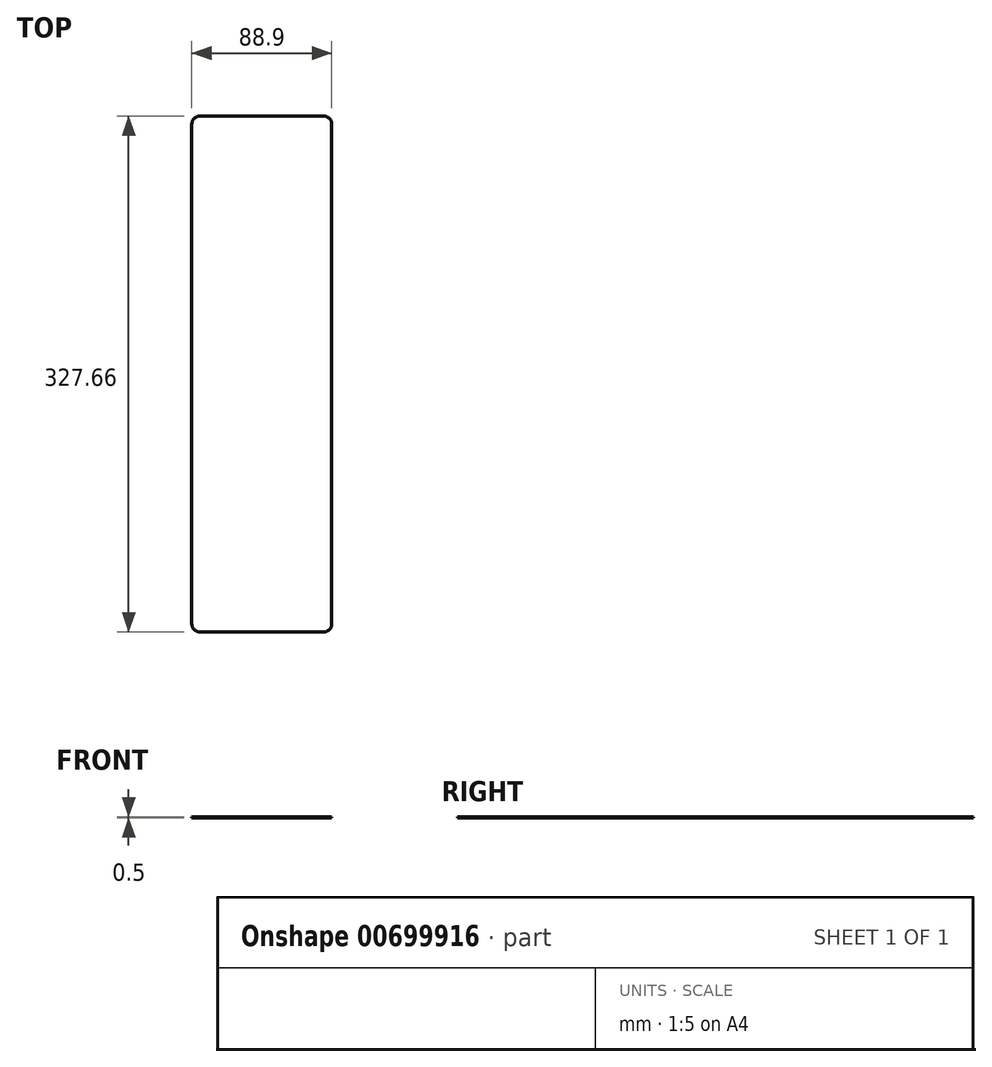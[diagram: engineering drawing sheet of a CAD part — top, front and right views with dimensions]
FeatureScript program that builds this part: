
annotation { "Feature Type Name" : "Feature", "Feature Type Description" : "" }
export const myFeature = defineFeature(function(context is Context, id is Id, definition is map)
    precondition{}
    {
        {
            var Q0;
            Q0=qCreatedBy(makeId("Top.planeOp"),FACE);
            var sketch = newSketch(context, id + "F0", { "sketchPlane" : qUnion([Q0])});
            skLineSegment(sketch, "E0.bottom", {"start": v(52.84, 164.88) * mm, "end": v(-36.06, 164.88) * mm});
            skLineSegment(sketch, "E0.top", {"start": v(52.84, -162.78) * mm, "end": v(-36.06, -162.78) * mm});
            skLineSegment(sketch, "E0.left", {"start": v(52.84, 164.88) * mm, "end": v(52.84, -162.78) * mm});
            skLineSegment(sketch, "E0.right", {"start": v(-36.06, 164.88) * mm, "end": v(-36.06, -162.78) * mm});
            skSolve(sketch);
        }
        {
            var Q0;
            Q0=makeQuery(id+"F0.imprint","IMPRINT",FACE,{"disambiguationData":[TD([[makeQuery(id+"F0.imprint","IMPRINT",EDGE,{"derivedFrom":sQuery(id+"F0.wireOp",EDGE,"E0.bottom")}),1.0]])]});
            extrude(context, id + "F1", {"entities" : qUnion([Q0]), "depth" : 0.5 * mm, "offsetDistance" : 25.4 * mm});
        }
        {
            var Q0;
            Q0=makeQuery(id+"F1.opExtrude","SWEPT_EDGE",EDGE,{"disambiguationData":[OSD([sQuery(id+"F0.wireOp",EDGE,"E0.bottom"),sQuery(id+"F0.wireOp",EDGE,"E0.right")])]});
            var Q1;
            Q1=makeQuery(id+"F1.opExtrude","SWEPT_EDGE",EDGE,{"disambiguationData":[OSD([sQuery(id+"F0.wireOp",EDGE,"E0.bottom"),sQuery(id+"F0.wireOp",EDGE,"E0.left")])]});
            var Q2;
            Q2=makeQuery(id+"F1.opExtrude","SWEPT_EDGE",EDGE,{"disambiguationData":[OSD([sQuery(id+"F0.wireOp",EDGE,"E0.top"),sQuery(id+"F0.wireOp",EDGE,"E0.right")])]});
            var Q3;
            Q3=makeQuery(id+"F1.opExtrude","SWEPT_EDGE",EDGE,{"disambiguationData":[OSD([sQuery(id+"F0.wireOp",EDGE,"E0.top"),sQuery(id+"F0.wireOp",EDGE,"E0.left")])]});
            fillet(context, id + "F2", {"entities" : qUnion([Q0, Q1, Q2, Q3]), "radius" : 5.08 * mm, "tangentPropagation" : true, "allowEdgeOverflow" : false});
        }
    });
